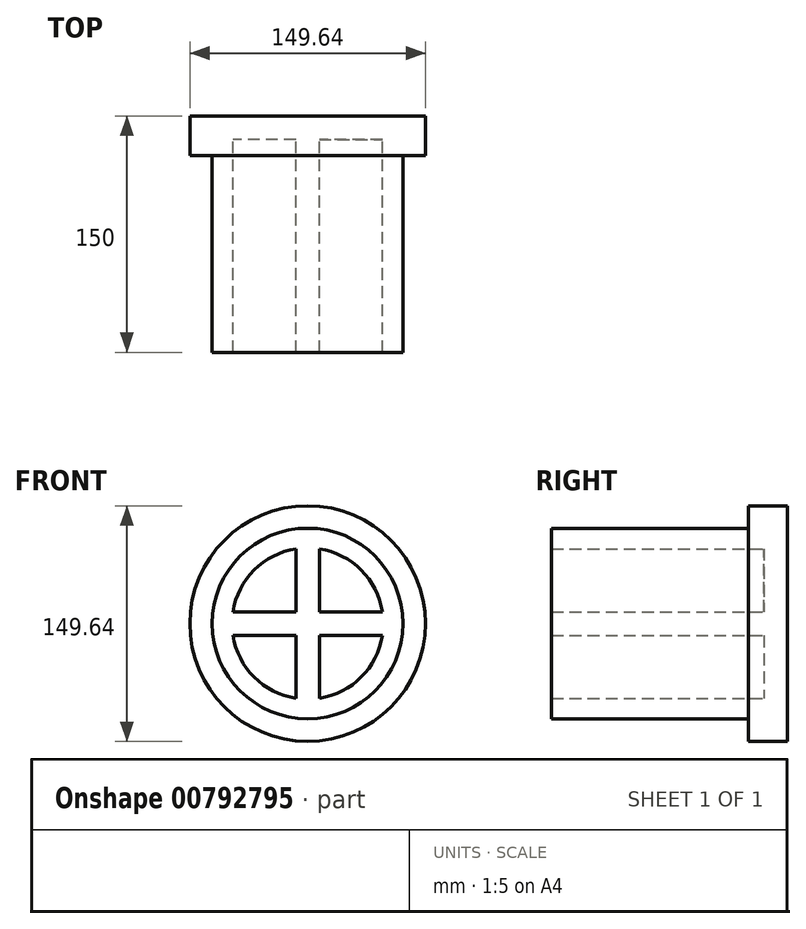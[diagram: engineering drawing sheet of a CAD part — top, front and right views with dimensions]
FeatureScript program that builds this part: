
annotation { "Feature Type Name" : "Feature", "Feature Type Description" : "" }
export const myFeature = defineFeature(function(context is Context, id is Id, definition is map)
    precondition{}
    {
        {
            var Q0;
            Q0=qCreatedBy(makeId("Front.planeOp"),FACE);
            var sketch = newSketch(context, id + "F0", { "sketchPlane" : qUnion([Q0])});
            skCircle(sketch, "E0", {"center": v(0, 0) * mm, "radius": 60.58 * mm});
            skCircle(sketch, "E1", {"center": v(0, 0) * mm, "radius": 51.7 * mm});
            skCircle(sketch, "E2", {"center": v(0, 0) * mm, "radius": 49.58 * mm});
            skCircle(sketch, "E3", {"center": v(0, 0) * mm, "radius": 48.08 * mm});
            skLineSegment(sketch, "E4", {"start": v(-7.5, 47.5) * mm, "end": v(-7.5, 7.5) * mm});
            skLineSegment(sketch, "E5", {"start": v(-7.5, 7.5) * mm, "end": v(-47.5, 7.5) * mm});
            skLineSegment(sketch, "E6", {"start": v(-7.5, -7.5) * mm, "end": v(-47.5, -7.5) * mm});
            skLineSegment(sketch, "E7", {"start": v(-7.5, -7.5) * mm, "end": v(-7.5, -47.5) * mm});
            skLineSegment(sketch, "E8", {"start": v(7.5, 47.5) * mm, "end": v(7.5, 7.5) * mm});
            skLineSegment(sketch, "E9", {"start": v(7.5, 7.5) * mm, "end": v(47.5, 7.5) * mm});
            skLineSegment(sketch, "E10", {"start": v(7.5, -7.5) * mm, "end": v(7.5, -47.5) * mm});
            skLineSegment(sketch, "E11", {"start": v(7.5, -7.5) * mm, "end": v(47.5, -7.5) * mm});
            skSolve(sketch);
        }
        {
            var Q0;
            Q0=makeQuery(id+"F0.imprint","IMPRINT",FACE,{"disambiguationData":[TD([[makeQuery(id+"F0.imprint","IMPRINT",EDGE,{"derivedFrom":sQuery(id+"F0.wireOp",EDGE,"E2")}),1.0]])]});
            var Q1;
            Q1=makeQuery(id+"F0.imprint","IMPRINT",FACE,{"disambiguationData":[TD([[makeQuery(id+"F0.imprint","IMPRINT",EDGE,{"derivedFrom":sQuery(id+"F0.wireOp",EDGE,"E1")}),1.0]])]});
            var Q2;
            Q2=makeQuery(id+"F0.imprint","IMPRINT",FACE,{"disambiguationData":[TD([[makeQuery(id+"F0.imprint","IMPRINT",EDGE,{"derivedFrom":sQuery(id+"F0.wireOp",EDGE,"E0")}),1.0]])]});
            var Q3;
            {var subQ4=sQuery(id+"F0.wireOp",EDGE,"E4");Q3=makeQuery(id+"F0.imprint","IMPRINT",FACE,{"disambiguationData":[TD([[makeQuery(id+"F0.imprint","IMPRINT",EDGE,{"derivedFrom":subQ4}),1.0]])]});}
            extrude(context, id + "F1", {"entities" : qUnion([Q0, Q1, Q2, Q3]), "depth" : 150 * mm, "offsetDistance" : 25 * mm});
        }
        {
            var Q0;
            Q0=qCreatedBy(makeId("Front.planeOp"),FACE);
            var sketch = newSketch(context, id + "F2", { "sketchPlane" : qUnion([Q0])});
            skCircle(sketch, "E12", {"center": v(0, 0) * mm, "radius": 74.82 * mm});
            skSolve(sketch);
        }
        {
            var Q0;
            Q0=makeQuery(id+"F2.imprint","IMPRINT",FACE,{"disambiguationData":[TD([[makeQuery(id+"F2.imprint","IMPRINT",EDGE,{"derivedFrom":sQuery(id+"F2.wireOp",EDGE,"E12")}),1.0]])]});
            extrude(context, id + "F3", {"entities" : qUnion([Q0]), "operationType" : NewBodyOperationType.ADD, "depth" : 25 * mm, "offsetDistance" : 25 * mm});
        }
        {
            var Q0;
            {var subQ0=sQuery(id+"F0.wireOp",EDGE,"E4");Q0=makeQuery(id+"F3.boolean.opBoolean","SPLIT",FACE,{"disambiguationData":[TD([makeQuery(id+"F1.opExtrude","SWEPT_FACE",FACE,{"disambiguationData":[OSD([subQ0])]})])],"derivedFrom":makeQuery(id+"F3.opExtrude","CAP_FACE",FACE,{"disambiguationData":[OSD([sQuery(id+"F2.wireOp",EDGE,"E12")])],"isStart":false})});}
            var Q1;
            {var subQ0=sQuery(id+"F0.wireOp",EDGE,"E8");Q1=makeQuery(id+"F3.boolean.opBoolean","SPLIT",FACE,{"disambiguationData":[TD([makeQuery(id+"F1.opExtrude","SWEPT_FACE",FACE,{"disambiguationData":[OSD([subQ0])]})])],"derivedFrom":makeQuery(id+"F3.opExtrude","CAP_FACE",FACE,{"disambiguationData":[OSD([sQuery(id+"F2.wireOp",EDGE,"E12")])],"isStart":false})});}
            var Q2;
            {var subQ0=sQuery(id+"F0.wireOp",EDGE,"E10");Q2=makeQuery(id+"F3.boolean.opBoolean","SPLIT",FACE,{"disambiguationData":[TD([makeQuery(id+"F1.opExtrude","SWEPT_FACE",FACE,{"disambiguationData":[OSD([subQ0])]})])],"derivedFrom":makeQuery(id+"F3.opExtrude","CAP_FACE",FACE,{"disambiguationData":[OSD([sQuery(id+"F2.wireOp",EDGE,"E12")])],"isStart":false})});}
            var Q3;
            {var subQ0=sQuery(id+"F0.wireOp",EDGE,"E6");Q3=makeQuery(id+"F3.boolean.opBoolean","SPLIT",FACE,{"disambiguationData":[TD([makeQuery(id+"F1.opExtrude","SWEPT_FACE",FACE,{"disambiguationData":[OSD([subQ0])]})])],"derivedFrom":makeQuery(id+"F3.opExtrude","CAP_FACE",FACE,{"disambiguationData":[OSD([sQuery(id+"F2.wireOp",EDGE,"E12")])],"isStart":false})});}
            extrude(context, id + "F4", {"entities" : qUnion([Q0, Q1, Q2, Q3]), "operationType" : NewBodyOperationType.REMOVE, "oppositeDirection" : true, "depth" : 10 * mm, "offsetDistance" : 25 * mm});
        }
    });
